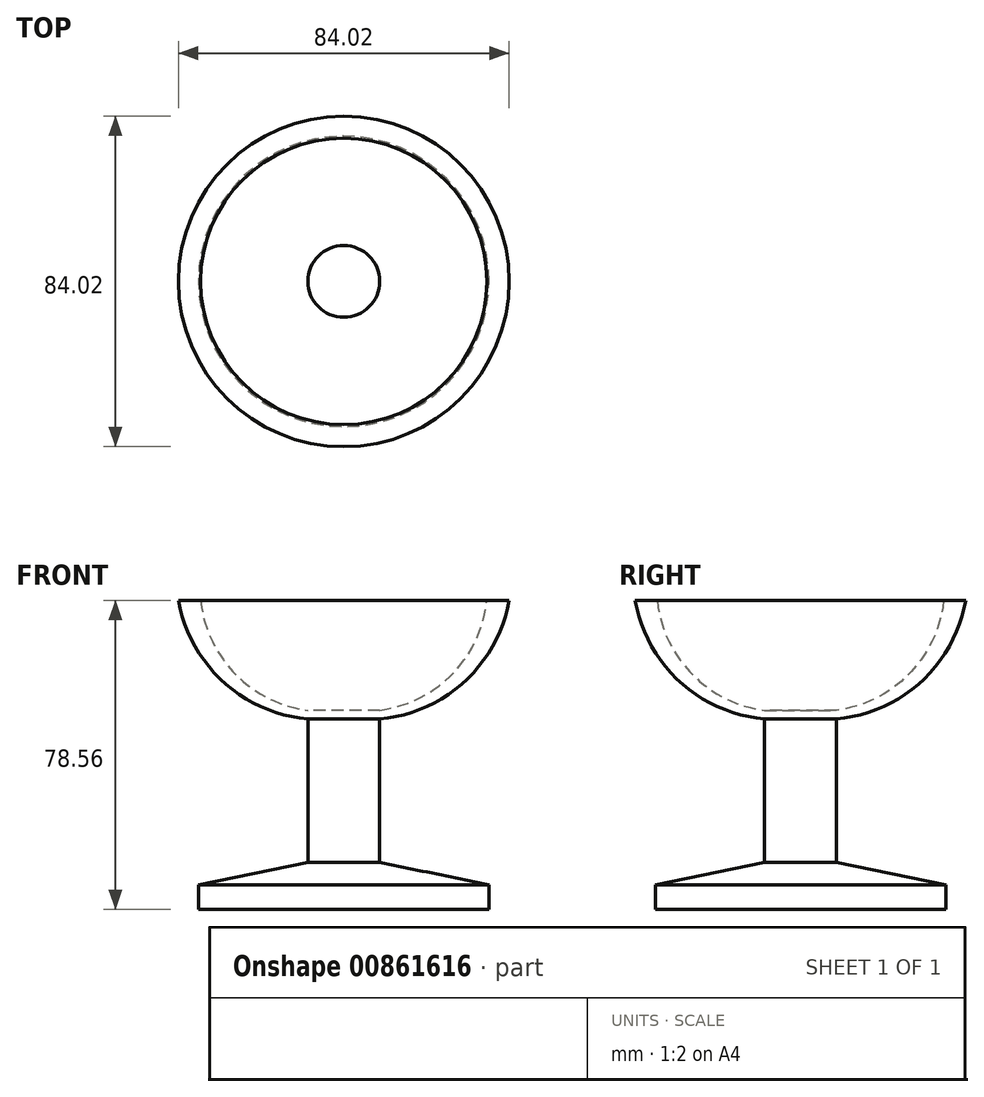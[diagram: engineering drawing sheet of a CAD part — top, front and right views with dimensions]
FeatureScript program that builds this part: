
annotation { "Feature Type Name" : "Feature", "Feature Type Description" : "" }
export const myFeature = defineFeature(function(context is Context, id is Id, definition is map)
    precondition{}
    {
        {
            var Q0;
            Q0=qCreatedBy(makeId("Front.planeOp"),FACE);
            var sketch = newSketch(context, id + "F0", { "sketchPlane" : qUnion([Q0])});
            skLineSegment(sketch, "E0", {"start": v(0, 0) * mm, "end": v(36.9, 0) * mm});
            skLineSegment(sketch, "E1", {"start": v(36.9, 0) * mm, "end": v(36.9, 6.3) * mm});
            skLineSegment(sketch, "E2", {"start": v(36.9, 6.3) * mm, "end": v(9.12, 11.93) * mm});
            skLineSegment(sketch, "E3", {"start": v(9.12, 11.93) * mm, "end": v(9.12, 48.4) * mm});
            skArc(sketch, "E4", {"start": v(9.12, 48.4) * mm, "mid": v(30.69, 57.9) * mm, "end": v(42, 78.56) * mm});
            skLineSegment(sketch, "E5", {"start": v(42, 78.56) * mm, "end": v(36.38, 78.56) * mm});
            skArc(sketch, "E6", {"start": v(9.12, 50.61) * mm, "mid": v(27.61, 59.85) * mm, "end": v(36.38, 78.56) * mm});
            skLineSegment(sketch, "E7", {"start": v(9.12, 50.61) * mm, "end": v(0, 50.61) * mm});
            skLineSegment(sketch, "E8", {"start": v(0, 50.61) * mm, "end": v(0, 0) * mm});
            skSolve(sketch);
        }
        {
            var Q0;
            Q0 = qSketchRegion(id + "F0", true);
            var Q1;
            Q1=sQuery(id+"F0.wireOp",EDGE,"E8");
            revolve(context, id + "F1", {"surfaceOperationType" : NewSurfaceOperationType.NEW, "entities" : qUnion([Q0]), "axis" : qUnion([Q1]), "revolveType" : RevolveType.FULL});
        }
    });
